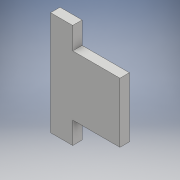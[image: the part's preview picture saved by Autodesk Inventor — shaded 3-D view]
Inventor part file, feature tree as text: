
AUTODESK INVENTOR PART (.ipt)
format: ipt  version: 2017 (Build 210142000, 142)  size: 97,792 bytes
history: native  units: mm
features: extrude x1, sketch x1
ambient origin geometry x8: Origin, YZ Plane, XZ Plane, XY Plane, X Axis, Y Axis, Z Axis, Center Point
bodies: Body1 (feature_tree)
feature tree (2):
  extrude  "Extrusion3"  Depth=19.0mm
  sketch  "Sketch3"  dims[d13=33.0mm d14=19.0mm d15=15.0mm d16=7.0mm d17=3.0mm d18=0.0mm]
